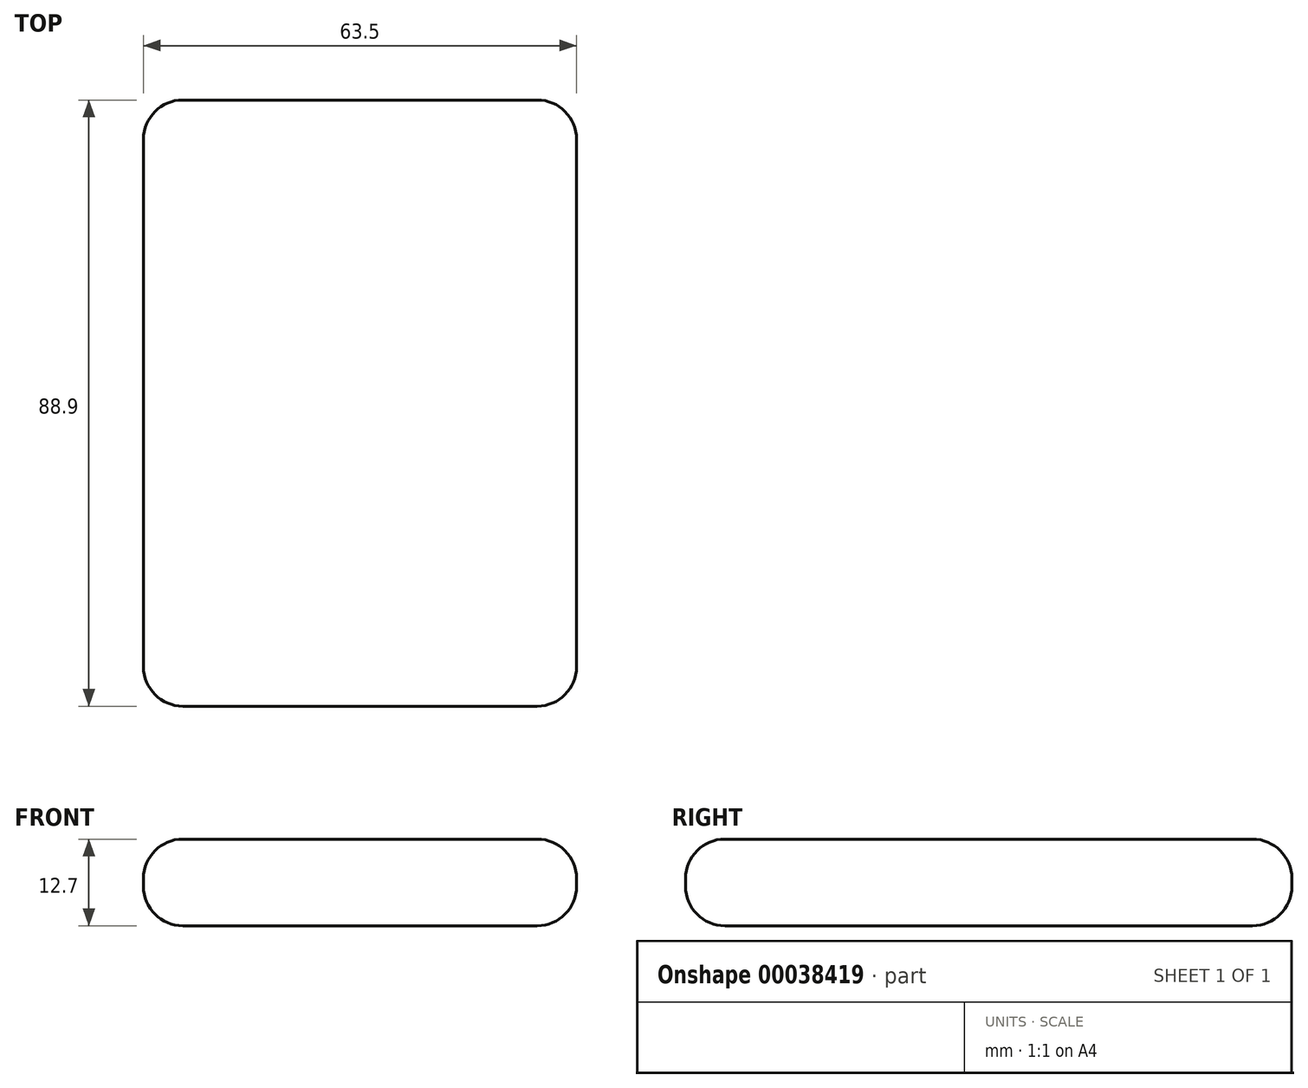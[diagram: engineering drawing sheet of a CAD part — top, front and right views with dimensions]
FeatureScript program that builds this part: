
annotation { "Feature Type Name" : "Feature", "Feature Type Description" : "" }
export const myFeature = defineFeature(function(context is Context, id is Id, definition is map)
    precondition{}
    {
        {
            var Q0;
            Q0=qCreatedBy(makeId("Top.planeOp"),FACE);
            var sketch = newSketch(context, id + "F0", { "sketchPlane" : qUnion([Q0])});
            skPoint(sketch, "E0", {"position": v(63.5, 0) * mm});
            skPoint(sketch, "E1", {"position": v(0, 88.9) * mm});
            skLineSegment(sketch, "E2.bottom", {"start": v(0, 88.9) * mm, "end": v(63.5, 88.9) * mm});
            skLineSegment(sketch, "E2.top", {"start": v(0, 0) * mm, "end": v(63.5, 0) * mm});
            skLineSegment(sketch, "E2.left", {"start": v(0, 88.9) * mm, "end": v(0, 0) * mm});
            skLineSegment(sketch, "E2.right", {"start": v(63.5, 88.9) * mm, "end": v(63.5, 0) * mm});
            skSolve(sketch);
        }
        {
            var Q0;
            Q0 = qSketchRegion(id + "F0", true);
            extrude(context, id + "F1", {"entities" : qUnion([Q0]), "depth" : 12.7 * mm});
        }
        {
            var Q0;
            Q0=makeQuery(id+"F1.opExtrude","CAP_EDGE",EDGE,{"disambiguationData":[OSD([sQuery(id+"F0.wireOp",EDGE,"E2.top")])],"isStart":false});
            var Q1;
            Q1=makeQuery(id+"F1.opExtrude","CAP_EDGE",EDGE,{"disambiguationData":[OSD([sQuery(id+"F0.wireOp",EDGE,"E2.right")])],"isStart":false});
            var Q2;
            Q2=makeQuery(id+"F1.opExtrude","CAP_EDGE",EDGE,{"disambiguationData":[OSD([sQuery(id+"F0.wireOp",EDGE,"E2.left")])],"isStart":false});
            var Q3;
            Q3=makeQuery(id+"F1.opExtrude","CAP_EDGE",EDGE,{"disambiguationData":[OSD([sQuery(id+"F0.wireOp",EDGE,"E2.bottom")])],"isStart":false});
            var Q4;
            Q4=makeQuery(id+"F1.opExtrude","CAP_EDGE",EDGE,{"disambiguationData":[OSD([sQuery(id+"F0.wireOp",EDGE,"E2.top")])],"isStart":true});
            var Q5;
            Q5=makeQuery(id+"F1.opExtrude","CAP_EDGE",EDGE,{"disambiguationData":[OSD([sQuery(id+"F0.wireOp",EDGE,"E2.right")])],"isStart":true});
            var Q6;
            Q6=makeQuery(id+"F1.opExtrude","CAP_EDGE",EDGE,{"disambiguationData":[OSD([sQuery(id+"F0.wireOp",EDGE,"E2.bottom")])],"isStart":true});
            var Q7;
            Q7=makeQuery(id+"F1.opExtrude","CAP_EDGE",EDGE,{"disambiguationData":[OSD([sQuery(id+"F0.wireOp",EDGE,"E2.left")])],"isStart":true});
            var Q8;
            Q8=makeQuery(id+"F1.opExtrude","SWEPT_EDGE",EDGE,{"disambiguationData":[OSD([sQuery(id+"F0.wireOp",EDGE,"E2.top"),sQuery(id+"F0.wireOp",EDGE,"E2.left")])]});
            var Q9;
            Q9=makeQuery(id+"F1.opExtrude","SWEPT_EDGE",EDGE,{"disambiguationData":[OSD([sQuery(id+"F0.wireOp",EDGE,"E2.top"),sQuery(id+"F0.wireOp",EDGE,"E2.right")])]});
            var Q10;
            Q10=makeQuery(id+"F1.opExtrude","SWEPT_EDGE",EDGE,{"disambiguationData":[OSD([sQuery(id+"F0.wireOp",EDGE,"E2.bottom"),sQuery(id+"F0.wireOp",EDGE,"E2.left")])]});
            var Q11;
            Q11=makeQuery(id+"F1.opExtrude","SWEPT_FACE",FACE,{"disambiguationData":[OSD([sQuery(id+"F0.wireOp",EDGE,"E2.right")])]});
            fillet(context, id + "F2", {"entities" : qUnion([Q0, Q1, Q2, Q3, Q4, Q5, Q6, Q7, Q8, Q9, Q10, Q11]), "radius" : 5.76 * mm, "tangentPropagation" : true, "allowEdgeOverflow" : false});
        }
    });
